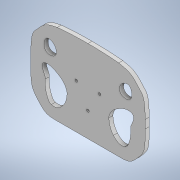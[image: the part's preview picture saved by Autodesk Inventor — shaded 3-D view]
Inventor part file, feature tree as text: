
AUTODESK INVENTOR PART (.ipt)
format: ipt  version: 2021 (Build 250183000, 183)  size: 181,760 bytes
history: native  units: in
note: dims shown in document units (in); Inventor stores cm internally (conversion verified against a paired STEP export)
features: extrude x1, sketch x1
ambient origin geometry x8: Origin, YZ Plane, XZ Plane, XY Plane, X Axis, Y Axis, Z Axis, Center Point
bodies: Solid1 (feature_tree)
feature tree (2):
  extrude  "Extrusion1"  [1 undecoded]
  sketch  "Sketch1"  dims[d1=0.3in d2=0.0in]
note: 1 required parameter value undecoded (feature->parameter linkage not recoverable at this tier; creation-order binding heuristic only, values carry confidence <= 0.55)
